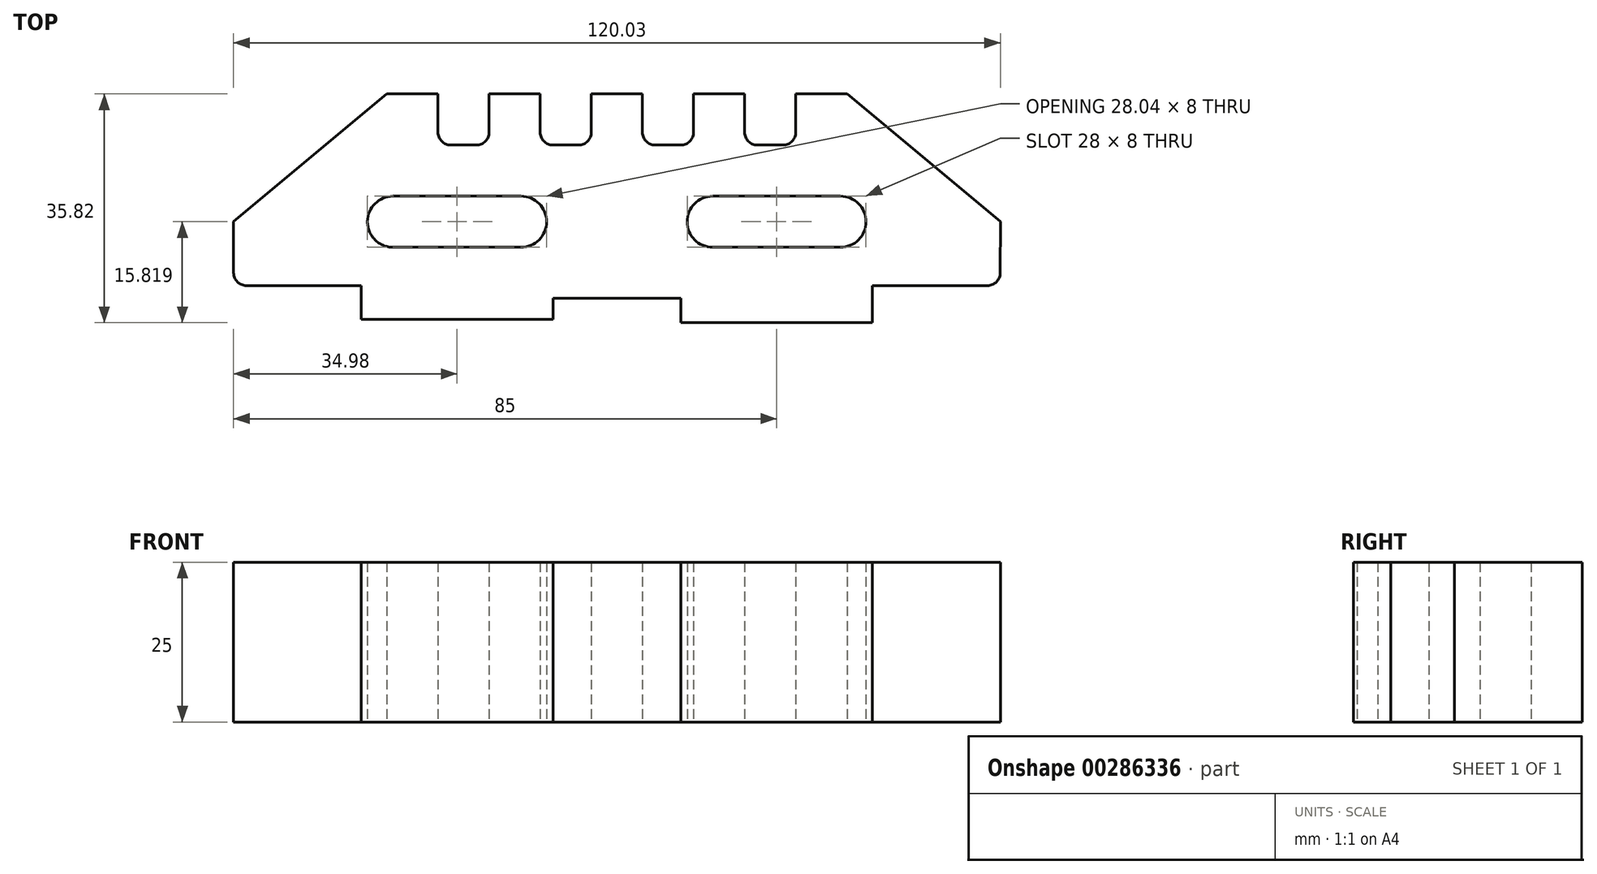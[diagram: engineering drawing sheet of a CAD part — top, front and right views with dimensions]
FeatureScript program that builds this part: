
annotation { "Feature Type Name" : "Feature", "Feature Type Description" : "" }
export const myFeature = defineFeature(function(context is Context, id is Id, definition is map)
    precondition{}
    {
        {
            var Q0;
            Q0=qCreatedBy(makeId("Top.planeOp"),FACE);
            var sketch = newSketch(context, id + "F0", { "sketchPlane" : qUnion([Q0])});
            skLineSegment(sketch, "E0", {"start": v(-75, 33.28) * mm, "end": v(-67, 33.28) * mm});
            skLineSegment(sketch, "E1", {"start": v(-67, 33.28) * mm, "end": v(-67, 27.28) * mm});
            skLineSegment(sketch, "E2", {"start": v(-65, 25.28) * mm, "end": v(-61, 25.28) * mm});
            skLineSegment(sketch, "E3", {"start": v(-59, 27.28) * mm, "end": v(-59, 33.28) * mm});
            skLineSegment(sketch, "E4", {"start": v(-59, 33.28) * mm, "end": v(-51, 33.28) * mm});
            skLineSegment(sketch, "E5", {"start": v(-51, 33.28) * mm, "end": v(-51, 27.28) * mm});
            skLineSegment(sketch, "E6", {"start": v(-49, 25.28) * mm, "end": v(-45, 25.28) * mm});
            skLineSegment(sketch, "E7", {"start": v(-43, 27.28) * mm, "end": v(-43, 33.28) * mm});
            skLineSegment(sketch, "E8", {"start": v(-43, 33.28) * mm, "end": v(-35, 33.28) * mm});
            skLineSegment(sketch, "E9", {"start": v(-35, 33.28) * mm, "end": v(-35, 27.28) * mm});
            skLineSegment(sketch, "E10", {"start": v(-33, 25.28) * mm, "end": v(-29, 25.28) * mm});
            skLineSegment(sketch, "E11", {"start": v(-27, 27.28) * mm, "end": v(-27, 33.28) * mm});
            skLineSegment(sketch, "E12", {"start": v(-27, 33.28) * mm, "end": v(-19, 33.28) * mm});
            skLineSegment(sketch, "E13", {"start": v(-19, 33.28) * mm, "end": v(-19, 27.28) * mm});
            skLineSegment(sketch, "E14", {"start": v(-17, 25.28) * mm, "end": v(-13, 25.28) * mm});
            skLineSegment(sketch, "E15", {"start": v(-11, 27.28) * mm, "end": v(-11, 33.28) * mm});
            skPoint(sketch, "E16.visualSharp", {"position": v(-67, 25.28) * mm});
            skArc(sketch, "E16.filletArc", {"start": v(-67, 27.28) * mm, "mid": v(-66.41, 25.86) * mm, "end": v(-65, 25.28) * mm});
            skPoint(sketch, "E17.visualSharp", {"position": v(-59, 25.28) * mm});
            skArc(sketch, "E17.filletArc", {"start": v(-61, 25.28) * mm, "mid": v(-59.59, 25.86) * mm, "end": v(-59, 27.28) * mm});
            skPoint(sketch, "E18.visualSharp", {"position": v(-51, 25.28) * mm});
            skArc(sketch, "E18.filletArc", {"start": v(-51, 27.28) * mm, "mid": v(-50.41, 25.86) * mm, "end": v(-49, 25.28) * mm});
            skPoint(sketch, "E19.visualSharp", {"position": v(-43, 25.28) * mm});
            skArc(sketch, "E19.filletArc", {"start": v(-45, 25.28) * mm, "mid": v(-43.59, 25.86) * mm, "end": v(-43, 27.28) * mm});
            skPoint(sketch, "E20.visualSharp", {"position": v(-35, 25.28) * mm});
            skArc(sketch, "E20.filletArc", {"start": v(-35, 27.28) * mm, "mid": v(-34.41, 25.86) * mm, "end": v(-33, 25.28) * mm});
            skPoint(sketch, "E21.visualSharp", {"position": v(-27, 25.28) * mm});
            skArc(sketch, "E21.filletArc", {"start": v(-29, 25.28) * mm, "mid": v(-27.59, 25.86) * mm, "end": v(-27, 27.28) * mm});
            skPoint(sketch, "E22.visualSharp", {"position": v(-19, 25.28) * mm});
            skArc(sketch, "E22.filletArc", {"start": v(-19, 27.28) * mm, "mid": v(-18.41, 25.86) * mm, "end": v(-17, 25.28) * mm});
            skPoint(sketch, "E23.visualSharp", {"position": v(-11, 25.28) * mm});
            skArc(sketch, "E23.filletArc", {"start": v(-13, 25.28) * mm, "mid": v(-11.59, 25.86) * mm, "end": v(-11, 27.28) * mm});
            skLineSegment(sketch, "E24", {"start": v(-75, 33.28) * mm, "end": v(-99, 13.28) * mm});
            skLineSegment(sketch, "E25", {"start": v(-99, 13.28) * mm, "end": v(-99, 5.28) * mm});
            skLineSegment(sketch, "E26", {"start": v(-97, 3.28) * mm, "end": v(-79, 3.28) * mm});
            skLineSegment(sketch, "E27", {"start": v(-79, 3.28) * mm, "end": v(-79, -2) * mm});
            skLineSegment(sketch, "E28", {"start": v(-79, -2) * mm, "end": v(-49, -2) * mm});
            skLineSegment(sketch, "E29", {"start": v(-49, -2) * mm, "end": v(-49, 1.28) * mm});
            skLineSegment(sketch, "E30", {"start": v(-49, 1.28) * mm, "end": v(-29, 1.28) * mm});
            skLineSegment(sketch, "E31", {"start": v(-29, 1.28) * mm, "end": v(-29, -2.54) * mm});
            skLineSegment(sketch, "E32", {"start": v(-29, -2.54) * mm, "end": v(1, -2.54) * mm});
            skLineSegment(sketch, "E33", {"start": v(1, -2.54) * mm, "end": v(1, 3.28) * mm});
            skLineSegment(sketch, "E34", {"start": v(1, 3.28) * mm, "end": v(19, 3.28) * mm});
            skLineSegment(sketch, "E35", {"start": v(-11, 33.28) * mm, "end": v(-2.97, 33.28) * mm});
            skLineSegment(sketch, "E36", {"start": v(-2.97, 33.28) * mm, "end": v(21.03, 13.28) * mm});
            skLineSegment(sketch, "E37", {"start": v(21.03, 13.28) * mm, "end": v(21, 5.27) * mm});
            skPoint(sketch, "E38.visualSharp", {"position": v(-99, 3.28) * mm});
            skArc(sketch, "E38.filletArc", {"start": v(-99, 5.28) * mm, "mid": v(-98.41, 3.86) * mm, "end": v(-97, 3.28) * mm});
            skLineSegment(sketch, "E39", {"start": v(-79, -2) * mm, "end": v(-79, 3.28) * mm});
            skLineSegment(sketch, "E40", {"start": v(-99, 13.28) * mm, "end": v(21.03, 13.28) * mm, "construction": true});
            skLineSegment(sketch, "E41", {"start": v(-75, 33.28) * mm, "end": v(-75, -2) * mm});
            skLineSegment(sketch, "E42", {"start": v(-2.97, 33.28) * mm, "end": v(-2.97, -2.54) * mm});
            skLineSegment(sketch, "E43", {"start": v(-29, 1.28) * mm, "end": v(-39, 1.28) * mm});
            skLineSegment(sketch, "E44", {"start": v(-39, 1.28) * mm, "end": v(-39, 33.28) * mm, "construction": true});
            skLineSegment(sketch, "E45", {"start": v(-39, 17.28) * mm, "end": v(-28, 17.28) * mm, "construction": true});
            skPoint(sketch, "E45.endSnap0", {"position": v(-39, 17.28) * mm});
            skLineSegment(sketch, "E46", {"start": v(-24, 17.28) * mm, "end": v(-4, 17.28) * mm});
            skLineSegment(sketch, "E47", {"start": v(-28, 13.28) * mm, "end": v(-28, 13.28) * mm});
            skLineSegment(sketch, "E48", {"start": v(-24, 9.28) * mm, "end": v(-4, 9.28) * mm});
            skLineSegment(sketch, "E49", {"start": v(0, 13.28) * mm, "end": v(0, 13.28) * mm});
            skLineSegment(sketch, "E50", {"start": v(-39, 17.28) * mm, "end": v(-39, 13.28) * mm});
            skPoint(sketch, "E51.visualSharp", {"position": v(-28, 17.28) * mm});
            skArc(sketch, "E51.filletArc", {"start": v(-24, 17.28) * mm, "mid": v(-26.83, 16.1) * mm, "end": v(-28, 13.28) * mm});
            skPoint(sketch, "E52.visualSharp", {"position": v(-28, 9.28) * mm});
            skArc(sketch, "E52.filletArc", {"start": v(-28, 13.28) * mm, "mid": v(-26.83, 10.45) * mm, "end": v(-24, 9.28) * mm});
            skPoint(sketch, "E53.visualSharp", {"position": v(0, 17.28) * mm});
            skArc(sketch, "E53.filletArc", {"start": v(0, 13.28) * mm, "mid": v(-1.17, 16.1) * mm, "end": v(-4, 17.28) * mm});
            skPoint(sketch, "E54.visualSharp", {"position": v(0, 9.28) * mm});
            skArc(sketch, "E54.filletArc", {"start": v(-4, 9.28) * mm, "mid": v(-1.17, 10.45) * mm, "end": v(0, 13.28) * mm});
            skLineSegment(sketch, "E55", {"start": v(-39, 17.28) * mm, "end": v(-50, 17.28) * mm, "construction": true});
            skLineSegment(sketch, "E56", {"start": v(-54, 17.28) * mm, "end": v(-74.04, 17.28) * mm});
            skLineSegment(sketch, "E57", {"start": v(-50, 13.28) * mm, "end": v(-50, 13.28) * mm});
            skLineSegment(sketch, "E58", {"start": v(-54, 9.28) * mm, "end": v(-74.04, 9.28) * mm});
            skLineSegment(sketch, "E59", {"start": v(-78.04, 13.32) * mm, "end": v(-78.04, 13.32) * mm});
            skPoint(sketch, "E60.visualSharp", {"position": v(-78, 17.28) * mm});
            skArc(sketch, "E60.filletArc", {"start": v(-74.04, 17.28) * mm, "mid": v(-76.85, 16.12) * mm, "end": v(-78.04, 13.32) * mm});
            skPoint(sketch, "E61.visualSharp", {"position": v(-78.08, 9.28) * mm});
            skArc(sketch, "E61.filletArc", {"start": v(-78.04, 13.32) * mm, "mid": v(-76.88, 10.47) * mm, "end": v(-74.04, 9.28) * mm});
            skPoint(sketch, "E62.visualSharp", {"position": v(-50, 17.28) * mm});
            skArc(sketch, "E62.filletArc", {"start": v(-50, 13.28) * mm, "mid": v(-51.17, 16.1) * mm, "end": v(-54, 17.28) * mm});
            skPoint(sketch, "E63.visualSharp", {"position": v(-50, 9.28) * mm});
            skArc(sketch, "E63.filletArc", {"start": v(-54, 9.28) * mm, "mid": v(-51.17, 10.45) * mm, "end": v(-50, 13.28) * mm});
            skPoint(sketch, "E64.visualSharp", {"position": v(21, 3.28) * mm});
            skArc(sketch, "E64.filletArc", {"start": v(19, 3.28) * mm, "mid": v(20.42, 3.86) * mm, "end": v(21, 5.27) * mm});
            skSolve(sketch);
        }
        {
            var Q0;
            Q0 = qSketchRegion(id + "F0", true);
            extrude(context, id + "F1", {"entities" : qUnion([Q0]), "depth" : 25 * mm});
        }
    });
